# Revit family: en-halla-saza-accessories-suspended-surfacerfa
name_source: partatom
category: Специальное оборудование
revit_build: Autodesk Revit 2017 (Build: 20160225_1515(x64)
units: mm (PartAtom-declared; Revit-internal decimal feet)

## family parameters
Заголовок OmniClass = General Luminaries, Non Directional
Номер OmniClass = 23.80.70.11.11
Общий = Нет
Основа = Грань
При загрузке вырезать с полостями = Нет
Размер круглого соединителя = Использовать диаметр
Тип детали = Нормальный
Точка расчета площади = Нет

## types (8) — shared parameters
Lighting height = 90 мм
Lighting length = 1000 мм
Lighting width = 79 мм
Material of luminaire = Aluminium
URL = www.halla.cz
Изготовитель = HALLA
Код по классификатору = D5020200
Отметка по умолчанию = 1000 мм

## per-type parameters (varying)
| type | Colour of luminaire | L | QR code | T | Tubus | X |
| 03-0003, E - joint 90°, metal | Aluminium - anodised | Да |  | Нет | Нет | Нет |
| 03-0003, W - joint 90°, metal | Aluminium - white | Да |  | Нет | Нет | Нет |
| 03-0001, E - body profile 1000mm | Aluminium - anodised | Нет |  | Нет | Да | Нет |
| 03-0001, W - body profile 1000mm | Aluminium - white | Нет |  | Нет | Да | Нет |
| 03-0004, W - joint T, metal | Aluminium - white | Нет |  | Да | Нет | Нет |
| 03-0004, E - joint T, metal | Aluminium - white | Нет |  | Да | Нет | Нет |
| 03-0005, E - joint X, metal | Aluminium - anodised | Нет |  | Нет | Нет | Да |
| 03-0005, W - joint X, metal | Aluminium - white | Нет | http://file-system.ru | Нет | Нет | Да |
